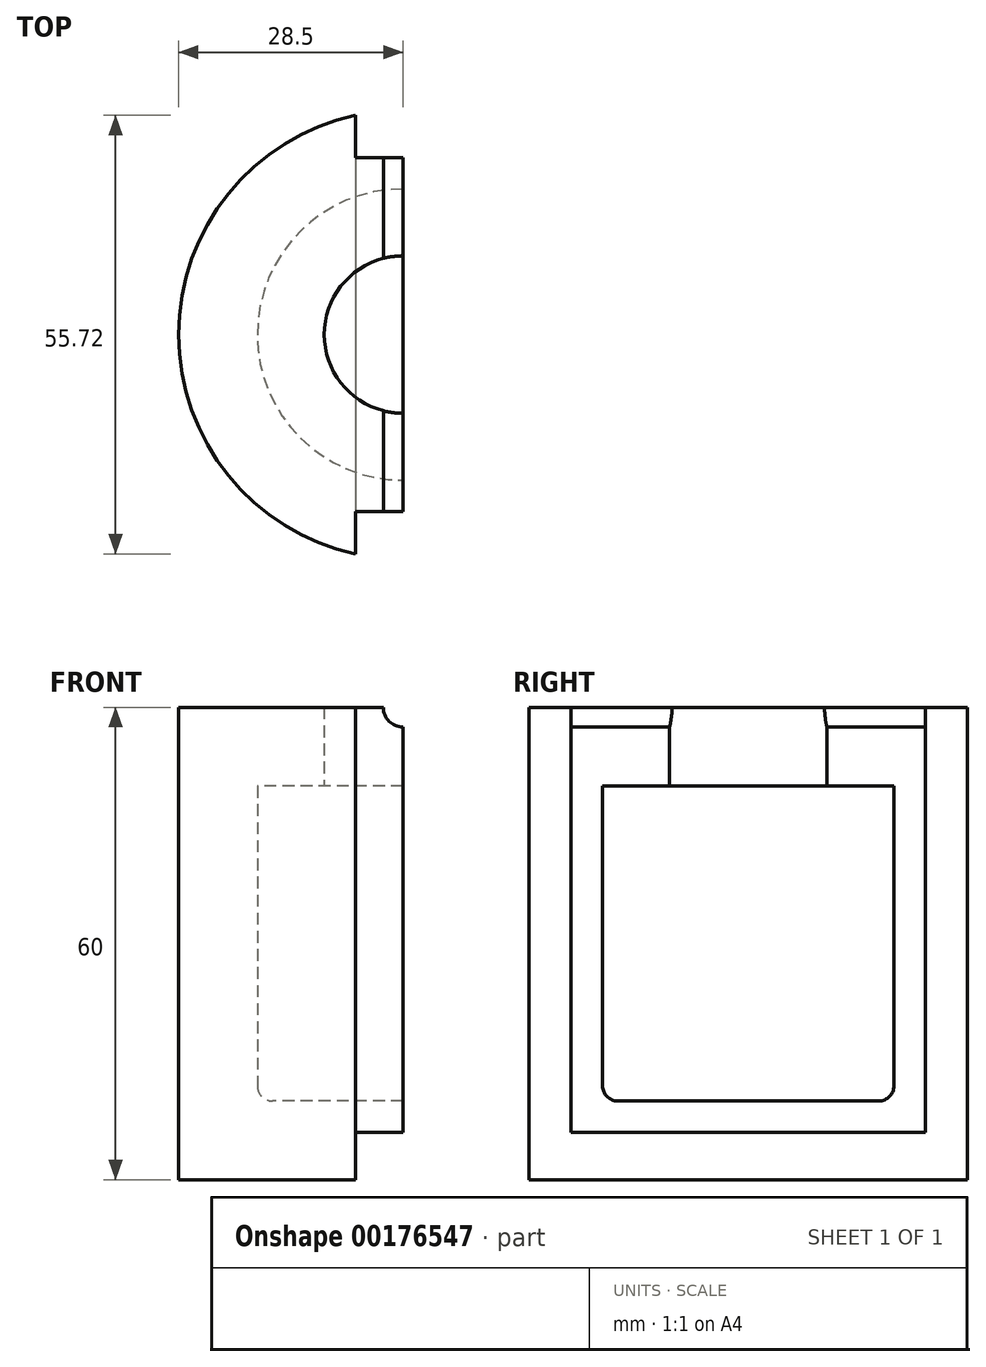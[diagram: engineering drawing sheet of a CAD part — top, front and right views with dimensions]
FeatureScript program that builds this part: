
annotation { "Feature Type Name" : "Feature", "Feature Type Description" : "" }
export const myFeature = defineFeature(function(context is Context, id is Id, definition is map)
    precondition{}
    {
        {
            var Q0;
            Q0=qCreatedBy(makeId("Front.planeOp"),FACE);
            var sketch = newSketch(context, id + "F0", { "sketchPlane" : qUnion([Q0])});
            skLineSegment(sketch, "E0.bottom", {"start": v(0, 0) * mm, "end": v(-18.5, 0) * mm});
            skLineSegment(sketch, "E0.top", {"start": v(0, 10) * mm, "end": v(-18.5, 10) * mm});
            skLineSegment(sketch, "E0.left", {"start": v(0, 0) * mm, "end": v(0, 10) * mm});
            skLineSegment(sketch, "E1.bottom", {"start": v(-18.5, 0) * mm, "end": v(-28.5, 0) * mm});
            skLineSegment(sketch, "E1.top", {"start": v(-18.5, 60) * mm, "end": v(-28.5, 60) * mm});
            skLineSegment(sketch, "E1.left", {"start": v(-18.5, 10) * mm, "end": v(-18.5, 50) * mm});
            skLineSegment(sketch, "E1.right", {"start": v(-28.5, 0) * mm, "end": v(-28.5, 60) * mm});
            skLineSegment(sketch, "E2.bottom", {"start": v(-18.5, 60) * mm, "end": v(-10, 60) * mm});
            skLineSegment(sketch, "E2.top", {"start": v(-18.5, 50) * mm, "end": v(-10, 50) * mm});
            skLineSegment(sketch, "E2.right", {"start": v(-10, 60) * mm, "end": v(-10, 50) * mm});
            skSolve(sketch);
        }
        {
            var Q0;
            Q0=makeQuery(id+"F0.imprint","IMPRINT",FACE,{"disambiguationData":[TD([[makeQuery(id+"F0.imprint","IMPRINT",EDGE,{"derivedFrom":sQuery(id+"F0.wireOp",EDGE,"E0.bottom")}),-1.0]])]});
            var Q1;
            Q1=sQuery(id+"F0.wireOp",EDGE,"E0.left");
            revolve(context, id + "F1", {"entities" : qUnion([Q0]), "axis" : qUnion([Q1]), "revolveType" : RevolveType.SYMMETRIC, "angle" : 180 * degree});
        }
        {
            var Q0;
            Q0=qCreatedBy(makeId("Front.planeOp"),FACE);
            var sketch = newSketch(context, id + "F2", { "sketchPlane" : qUnion([Q0])});
            skLineSegment(sketch, "E3", {"start": v(-28.5, 0) * mm, "end": v(-28.5, 60) * mm});
            skCircle(sketch, "E4", {"center": v(0, 60) * mm, "radius": 2.5 * mm});
            skSolve(sketch);
        }
        {
            var Q0;
            Q0=makeQuery(id+"F2.imprint","IMPRINT",FACE,{"disambiguationData":[TD([[makeQuery(id+"F2.imprint","IMPRINT",EDGE,{"derivedFrom":sQuery(id+"F2.wireOp",EDGE,"E4")}),1.0]])]});
            extrude(context, id + "F3", {"entities" : qUnion([Q0]), "operationType" : NewBodyOperationType.REMOVE, "endBound" : BoundingType.THROUGH_ALL, "oppositeDirection" : true, "depth" : 25.4 * mm, "hasSecondDirection" : true, "secondDirectionBound" : SecondDirectionBoundingType.THROUGH_ALL, "secondDirectionOppositeDirection" : false, "secondDirectionDepth" : 25.4 * mm});
        }
        {
            var Q0;
            Q0=makeQuery(id+"F1.opRevolve","SWEPT_EDGE",EDGE,{"disambiguationData":[OSD([sQuery(id+"F0.wireOp",EDGE,"E0.top"),sQuery(id+"F0.wireOp",EDGE,"E1.left")])]});
            fillet(context, id + "F4", {"entities" : qUnion([Q0]), "radius" : 1.9 * mm, "tangentPropagation" : true, "allowEdgeOverflow" : false});
        }
        {
            var Q0;
            Q0=makeQuery(id+"F1.opRevolve","CAP_FACE",FACE,{"disambiguationData":[OSD([sQuery(id+"F0.wireOp",EDGE,"E0.bottom"),sQuery(id+"F0.wireOp",EDGE,"E0.top"),sQuery(id+"F0.wireOp",EDGE,"E0.left"),sQuery(id+"F0.wireOp",EDGE,"E1.bottom"),sQuery(id+"F0.wireOp",EDGE,"E1.top"),sQuery(id+"F0.wireOp",EDGE,"E1.left"),sQuery(id+"F0.wireOp",EDGE,"E1.right"),sQuery(id+"F0.wireOp",EDGE,"E2.bottom"),sQuery(id+"F0.wireOp",EDGE,"E2.top"),sQuery(id+"F0.wireOp",EDGE,"E2.right")])],"isStart":false});
            var sketch = newSketch(context, id + "F5", { "sketchPlane" : qUnion([Q0])});
            skLineSegment(sketch, "E5.bottom", {"start": v(-22.5, 60) * mm, "end": v(-28.5, 60) * mm});
            skLineSegment(sketch, "E5.top", {"start": v(-22.5, 56) * mm, "end": v(-28.5, 56) * mm});
            skLineSegment(sketch, "E5.left", {"start": v(-22.5, 60) * mm, "end": v(-22.5, 56) * mm});
            skLineSegment(sketch, "E5.right", {"start": v(-28.5, 60) * mm, "end": v(-28.5, 56) * mm});
            skLineSegment(sketch, "E6.bottom", {"start": v(22.5, 60) * mm, "end": v(28.5, 60) * mm});
            skLineSegment(sketch, "E6.top", {"start": v(22.5, 56) * mm, "end": v(28.5, 56) * mm});
            skLineSegment(sketch, "E6.left", {"start": v(22.5, 60) * mm, "end": v(22.5, 56) * mm});
            skLineSegment(sketch, "E6.right", {"start": v(28.5, 60) * mm, "end": v(28.5, 56) * mm});
            skLineSegment(sketch, "E7.bottom", {"start": v(-22.5, 0) * mm, "end": v(-28.5, 0) * mm});
            skLineSegment(sketch, "E7.left", {"start": v(-22.5, 0) * mm, "end": v(-22.5, 56) * mm});
            skLineSegment(sketch, "E7.right", {"start": v(-28.5, 0) * mm, "end": v(-28.5, 56) * mm});
            skLineSegment(sketch, "E8.top", {"start": v(22.5, 0) * mm, "end": v(28.5, 0) * mm});
            skLineSegment(sketch, "E8.left", {"start": v(22.5, 0) * mm, "end": v(22.5, 56) * mm});
            skLineSegment(sketch, "E8.right", {"start": v(28.5, 0) * mm, "end": v(28.5, 56) * mm});
            skLineSegment(sketch, "E9.bottom", {"start": v(22.5, 6) * mm, "end": v(-22.5, 6) * mm});
            skLineSegment(sketch, "E9.top", {"start": v(22.5, 0) * mm, "end": v(-22.5, 0) * mm});
            skLineSegment(sketch, "E9.left", {"start": v(22.5, 6) * mm, "end": v(22.5, 0) * mm});
            skLineSegment(sketch, "E9.right", {"start": v(-22.5, 6) * mm, "end": v(-22.5, 0) * mm});
            skSolve(sketch);
        }
        {
            var Q0;
            Q0=makeQuery(id+"F5.imprint","IMPRINT",FACE,{"disambiguationData":[TD([[makeQuery(id+"F5.imprint","IMPRINT",EDGE,{"derivedFrom":sQuery(id+"F5.wireOp",EDGE,"E5.bottom")}),-1.0]])]});
            var Q1;
            Q1=makeQuery(id+"F5.imprint","IMPRINT",FACE,{"disambiguationData":[TD([[makeQuery(id+"F5.imprint","IMPRINT",EDGE,{"derivedFrom":sQuery(id+"F5.wireOp",EDGE,"E7.bottom")}),-1.0]])]});
            var Q2;
            Q2=makeQuery(id+"F5.imprint","IMPRINT",FACE,{"disambiguationData":[TD([[makeQuery(id+"F5.imprint","IMPRINT",EDGE,{"derivedFrom":sQuery(id+"F5.wireOp",EDGE,"E6.bottom")}),-1.0]])]});
            var Q3;
            Q3=makeQuery(id+"F5.imprint","IMPRINT",FACE,{"disambiguationData":[TD([[makeQuery(id+"F5.imprint","IMPRINT",EDGE,{"derivedFrom":sQuery(id+"F5.wireOp",EDGE,"E6.top")}),-1.0]])]});
            var Q4;
            Q4=makeQuery(id+"F5.imprint","IMPRINT",FACE,{"disambiguationData":[TD([[makeQuery(id+"F5.imprint","IMPRINT",EDGE,{"derivedFrom":sQuery(id+"F5.wireOp",EDGE,"E9.bottom")}),1.0]])]});
            var Q5;
            {var subQ0=sQuery(id+"F5.wireOp",EDGE,"E5.bottom");Q5=makeQuery(id+"F5.imprint","IMPRINT",FACE,{"disambiguationData":[TD([[makeQuery(id+"F5.imprint","IMPRINT",EDGE,{"derivedFrom":subQ0}),1.0]])]});}
            var Q6;
            {var subQ0=sQuery(id+"F5.wireOp",EDGE,"E6.top");Q6=makeQuery(id+"F5.imprint","IMPRINT",FACE,{"disambiguationData":[TD([[makeQuery(id+"F5.imprint","IMPRINT",EDGE,{"derivedFrom":subQ0}),1.0]])]});}
            var Q7;
            {var subQ0=sQuery(id+"F5.wireOp",EDGE,"E5.top");Q7=makeQuery(id+"F5.imprint","IMPRINT",FACE,{"disambiguationData":[TD([[makeQuery(id+"F5.imprint","IMPRINT",EDGE,{"derivedFrom":subQ0}),-1.0]])]});}
            extrude(context, id + "F6", {"entities" : qUnion([Q0, Q1, Q2, Q3, Q4, Q5, Q6, Q7]), "operationType" : NewBodyOperationType.REMOVE, "oppositeDirection" : true, "depth" : 6 * mm});
        }
    });
